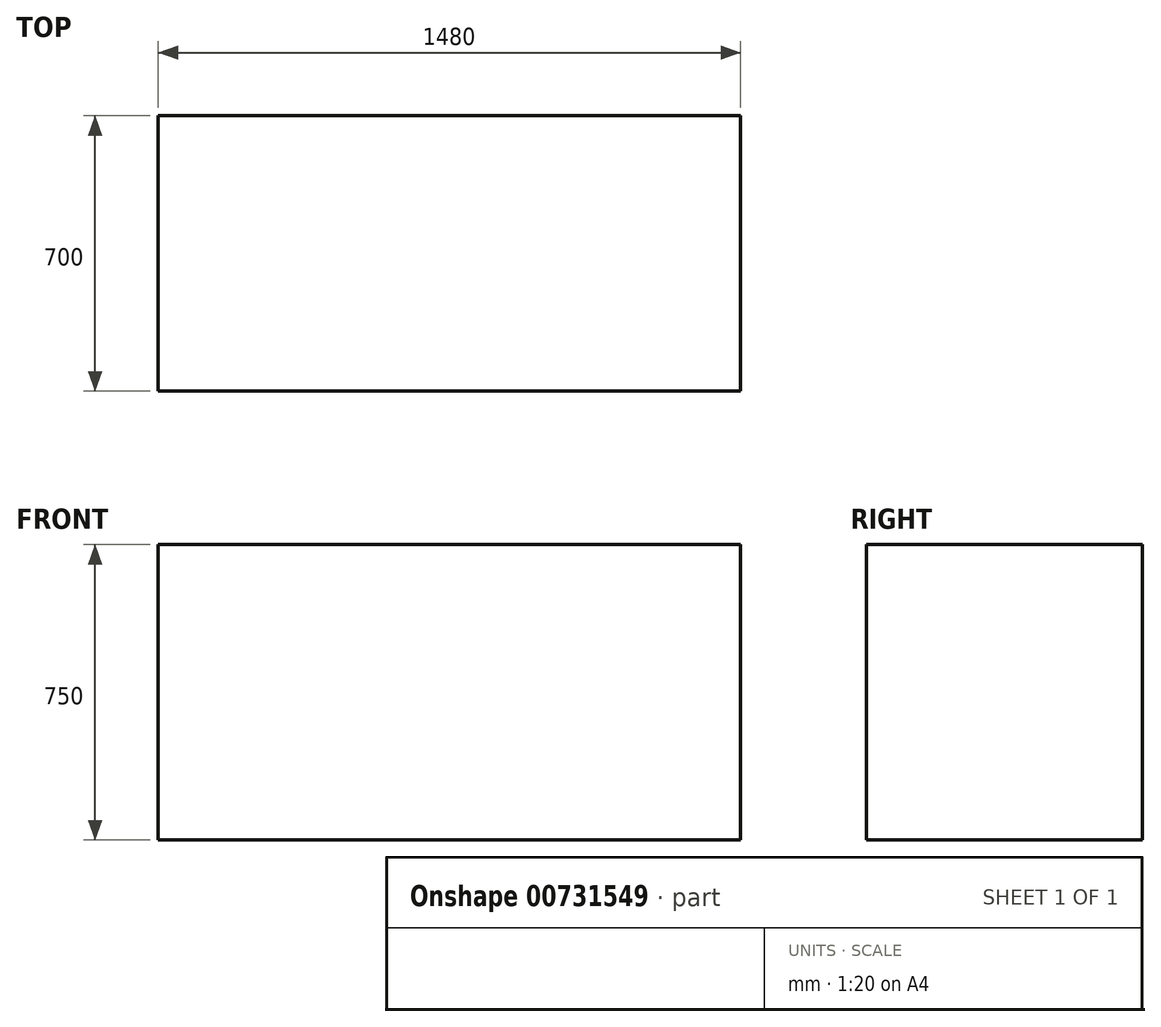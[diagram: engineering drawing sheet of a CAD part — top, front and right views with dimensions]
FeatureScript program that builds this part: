
annotation { "Feature Type Name" : "Feature", "Feature Type Description" : "" }
export const myFeature = defineFeature(function(context is Context, id is Id, definition is map)
    precondition{}
    {
        {
            var Q0;
            Q0=qCreatedBy(makeId("Top.planeOp"),FACE);
            var sketch = newSketch(context, id + "F0", { "sketchPlane" : qUnion([Q0])});
            skLineSegment(sketch, "E0", {"start": v(0, 3530) * mm, "end": v(0, 0) * mm});
            skLineSegment(sketch, "E1", {"start": v(0, 0) * mm, "end": v(3200, 0) * mm});
            skLineSegment(sketch, "E2", {"start": v(3200, 0) * mm, "end": v(3200, 230) * mm});
            skLineSegment(sketch, "E3", {"start": v(3200, 230) * mm, "end": v(3720, 230) * mm});
            skLineSegment(sketch, "E4", {"start": v(3720, 230) * mm, "end": v(3720, 680) * mm});
            skLineSegment(sketch, "E5", {"start": v(3720, 680) * mm, "end": v(4240, 680) * mm});
            skLineSegment(sketch, "E6", {"start": v(4240, 680) * mm, "end": v(4240, 2510) * mm});
            skLineSegment(sketch, "E7", {"start": v(4240, 2510) * mm, "end": v(3720, 2510) * mm});
            skLineSegment(sketch, "E8", {"start": v(3720, 2510) * mm, "end": v(3720, 3310) * mm});
            skLineSegment(sketch, "E9", {"start": v(3720, 3310) * mm, "end": v(3200, 3310) * mm});
            skLineSegment(sketch, "E10", {"start": v(3200, 3310) * mm, "end": v(3200, 3530) * mm});
            skLineSegment(sketch, "E11", {"start": v(3200, 3530) * mm, "end": v(0, 3530) * mm});
            skSolve(sketch);
        }
        {
            var Q0;
            Q0=makeQuery(id+"F0.imprint","IMPRINT",FACE,{"disambiguationData":[TD([[makeQuery(id+"F0.imprint","IMPRINT",EDGE,{"derivedFrom":sQuery(id+"F0.wireOp",EDGE,"E0")}),1.0]])]});
            var sketch = newSketch(context, id + "F1", { "sketchPlane" : qUnion([Q0])});
            skLineSegment(sketch, "E12.bottom", {"start": v(-150, 3130) * mm, "end": v(150, 3130) * mm});
            skLineSegment(sketch, "E12.top", {"start": v(-150, 2280) * mm, "end": v(150, 2280) * mm});
            skLineSegment(sketch, "E12.left", {"start": v(-150, 3130) * mm, "end": v(-150, 2280) * mm});
            skLineSegment(sketch, "E12.right", {"start": v(150, 3130) * mm, "end": v(150, 2280) * mm});
            skSolve(sketch);
        }
        {
            var Q0;
            Q0=makeQuery(id+"F0.imprint","IMPRINT",FACE,{"disambiguationData":[TD([[makeQuery(id+"F0.imprint","IMPRINT",EDGE,{"derivedFrom":sQuery(id+"F0.wireOp",EDGE,"E0")}),1.0]])]});
            var sketch = newSketch(context, id + "F2", { "sketchPlane" : qUnion([Q0])});
            skLineSegment(sketch, "E13.bottom", {"start": v(0, 1180) * mm, "end": v(-1500, 1180) * mm});
            skLineSegment(sketch, "E13.top", {"start": v(0, 4530) * mm, "end": v(-1500, 4530) * mm});
            skLineSegment(sketch, "E13.left", {"start": v(0, 1180) * mm, "end": v(0, 4530) * mm});
            skLineSegment(sketch, "E13.right", {"start": v(-1500, 1180) * mm, "end": v(-1500, 4530) * mm});
            skSolve(sketch);
        }
        {
            var Q0;
            Q0=makeQuery(id+"F0.imprint","IMPRINT",FACE,{"disambiguationData":[TD([[makeQuery(id+"F0.imprint","IMPRINT",EDGE,{"derivedFrom":sQuery(id+"F0.wireOp",EDGE,"E0")}),1.0]])]});
            var sketch = newSketch(context, id + "F3", { "sketchPlane" : qUnion([Q0])});
            skLineSegment(sketch, "E14.bottom", {"start": v(-1350, 3130) * mm, "end": v(-1650, 3130) * mm});
            skLineSegment(sketch, "E14.top", {"start": v(-1350, 3930) * mm, "end": v(-1650, 3930) * mm});
            skLineSegment(sketch, "E14.left", {"start": v(-1350, 3130) * mm, "end": v(-1350, 3930) * mm});
            skLineSegment(sketch, "E14.right", {"start": v(-1650, 3130) * mm, "end": v(-1650, 3930) * mm});
            skPoint(sketch, "E14.middle", {"position": v(-1500, 3530) * mm});
            skSolve(sketch);
        }
        {
            var Q0;
            Q0=makeQuery(id+"F0.imprint","IMPRINT",FACE,{"disambiguationData":[TD([[makeQuery(id+"F0.imprint","IMPRINT",EDGE,{"derivedFrom":sQuery(id+"F0.wireOp",EDGE,"E0")}),1.0]])]});
            var sketch = newSketch(context, id + "F4", { "sketchPlane" : qUnion([Q0])});
            skLineSegment(sketch, "E15", {"start": v(0, 7310) * mm, "end": v(0, 3530) * mm});
            skLineSegment(sketch, "E16", {"start": v(0, 3530) * mm, "end": v(3800, 3530) * mm});
            skLineSegment(sketch, "E17", {"start": v(3800, 3530) * mm, "end": v(3800, 4130) * mm});
            skLineSegment(sketch, "E18", {"start": v(3800, 4130) * mm, "end": v(4330, 4130) * mm});
            skLineSegment(sketch, "E19", {"start": v(4330, 4130) * mm, "end": v(4330, 6130) * mm});
            skLineSegment(sketch, "E20", {"start": v(4330, 6130) * mm, "end": v(3800, 6130) * mm});
            skLineSegment(sketch, "E21", {"start": v(3800, 6130) * mm, "end": v(3800, 7310) * mm});
            skLineSegment(sketch, "E22", {"start": v(3800, 7310) * mm, "end": v(0, 7310) * mm});
            skSolve(sketch);
        }
        {
            var Q0;
            Q0=makeQuery(id+"F0.imprint","IMPRINT",FACE,{"disambiguationData":[TD([[makeQuery(id+"F0.imprint","IMPRINT",EDGE,{"derivedFrom":sQuery(id+"F0.wireOp",EDGE,"E0")}),1.0]])]});
            var sketch = newSketch(context, id + "F5", { "sketchPlane" : qUnion([Q0])});
            skLineSegment(sketch, "E23.bottom", {"start": v(-200, 1710) * mm, "end": v(0, 1710) * mm});
            skLineSegment(sketch, "E23.top", {"start": v(-200, 1260) * mm, "end": v(0, 1260) * mm});
            skLineSegment(sketch, "E23.left", {"start": v(-200, 1710) * mm, "end": v(-200, 1260) * mm});
            skLineSegment(sketch, "E23.right", {"start": v(0, 1710) * mm, "end": v(0, 1260) * mm});
            skPoint(sketch, "E23.middle", {"position": v(-100, 1485) * mm});
            skSolve(sketch);
        }
        {
            var Q0;
            {var subQ3=sQuery(id+"F4.wireOp",EDGE,"E15");Q0=makeQuery(id+"F4.imprint","IMPRINT",FACE,{"disambiguationData":[TD([[makeQuery(id+"F4.imprint","IMPRINT",EDGE,{"derivedFrom":subQ3}),1.0]])]});}
            var sketch = newSketch(context, id + "F6", { "sketchPlane" : qUnion([Q0])});
            skLineSegment(sketch, "E24.bottom", {"start": v(-350, 4380) * mm, "end": v(-1150, 4380) * mm});
            skLineSegment(sketch, "E24.top", {"start": v(-350, 4680) * mm, "end": v(-1150, 4680) * mm});
            skLineSegment(sketch, "E24.left", {"start": v(-350, 4380) * mm, "end": v(-350, 4680) * mm});
            skLineSegment(sketch, "E24.right", {"start": v(-1150, 4380) * mm, "end": v(-1150, 4680) * mm});
            skPoint(sketch, "E24.middle", {"position": v(-750, 4530) * mm});
            skSolve(sketch);
        }
        {
            var Q0;
            Q0=makeQuery(id+"F0.imprint","IMPRINT",FACE,{"disambiguationData":[TD([[makeQuery(id+"F0.imprint","IMPRINT",EDGE,{"derivedFrom":sQuery(id+"F0.wireOp",EDGE,"E0")}),1.0]])]});
            var sketch = newSketch(context, id + "F7", { "sketchPlane" : qUnion([Q0])});
            skLineSegment(sketch, "E25.bottom", {"start": v(-1500, 2450) * mm, "end": v(-5240, 2450) * mm});
            skLineSegment(sketch, "E25.top", {"start": v(-1500, 4530) * mm, "end": v(-5240, 4530) * mm});
            skLineSegment(sketch, "E25.left", {"start": v(-1500, 2450) * mm, "end": v(-1500, 4530) * mm});
            skLineSegment(sketch, "E25.right", {"start": v(-5240, 2450) * mm, "end": v(-5240, 4530) * mm});
            skPoint(sketch, "E25.middle", {"position": v(-3370, 3490) * mm});
            skSolve(sketch);
        }
        {
            var Q0;
            Q0=makeQuery(id+"F0.imprint","IMPRINT",FACE,{"disambiguationData":[TD([[makeQuery(id+"F0.imprint","IMPRINT",EDGE,{"derivedFrom":sQuery(id+"F0.wireOp",EDGE,"E0")}),1.0]])]});
            var sketch = newSketch(context, id + "F8", { "sketchPlane" : qUnion([Q0])});
            skLineSegment(sketch, "E26.bottom", {"start": v(900, 3680) * mm, "end": v(1650, 3680) * mm});
            skLineSegment(sketch, "E26.top", {"start": v(900, 3380) * mm, "end": v(1650, 3380) * mm});
            skLineSegment(sketch, "E26.left", {"start": v(900, 3680) * mm, "end": v(900, 3380) * mm});
            skLineSegment(sketch, "E26.right", {"start": v(1650, 3680) * mm, "end": v(1650, 3380) * mm});
            skSolve(sketch);
        }
        {
            var Q0;
            Q0=makeQuery(id+"F7.imprint","IMPRINT",FACE,{"disambiguationData":[TD([[makeQuery(id+"F7.imprint","IMPRINT",EDGE,{"derivedFrom":makeQuery(id+"F0.imprint","IMPRINT",EDGE,{"derivedFrom":sQuery(id+"F0.wireOp",EDGE,"E0")})}),1.0]])]});
            var sketch = newSketch(context, id + "F9", { "sketchPlane" : qUnion([Q0])});
            skLineSegment(sketch, "E27", {"start": v(-5240, 7080) * mm, "end": v(-5240, 4780) * mm});
            skLineSegment(sketch, "E28", {"start": v(-5240, 4780) * mm, "end": v(-4210, 4780) * mm});
            skLineSegment(sketch, "E29", {"start": v(-4210, 4780) * mm, "end": v(-4210, 4530) * mm});
            skLineSegment(sketch, "E30", {"start": v(-4210, 4530) * mm, "end": v(-320, 4530) * mm});
            skLineSegment(sketch, "E31", {"start": v(-320, 4530) * mm, "end": v(-320, 7080) * mm});
            skLineSegment(sketch, "E32", {"start": v(-320, 7080) * mm, "end": v(-5240, 7080) * mm});
            skSolve(sketch);
        }
        {
            var Q0;
            {var subQ0=sQuery(id+"F8.wireOp",EDGE,"E26.top");Q0=makeQuery(id+"F8.imprint","IMPRINT",FACE,{"disambiguationData":[TD([[makeQuery(id+"F8.imprint","IMPRINT",EDGE,{"derivedFrom":subQ0}),-1.0]])]});}
            var sketch = newSketch(context, id + "F10", { "sketchPlane" : qUnion([Q0])});
            skLineSegment(sketch, "E33.bottom", {"start": v(1668.4, 3495.11) * mm, "end": v(3148.4, 3495.11) * mm});
            skLineSegment(sketch, "E33.top", {"start": v(1668.4, 2795.11) * mm, "end": v(3148.4, 2795.11) * mm});
            skLineSegment(sketch, "E33.left", {"start": v(1668.4, 3495.11) * mm, "end": v(1668.4, 2795.11) * mm});
            skLineSegment(sketch, "E33.right", {"start": v(3148.4, 3495.11) * mm, "end": v(3148.4, 2795.11) * mm});
            skSolve(sketch);
        }
        {
            var Q0;
            Q0 = qSketchRegion(id + "F10", true);
            extrude(context, id + "F11", {"entities" : qUnion([Q0]), "depth" : 750 * mm, "offsetDistance" : 25 * mm});
        }
    });
